# Revit family: CENTUM Gleitunterlage mit Abhebesicherung stehend_
name_source: partatom
category: HLS-Bauteile
revit_build: Autodesk Revit 2017 (Build: 20190508_0315(x64)
units: mm (PartAtom-declared; Revit-internal decimal feet)

## family parameters
Arbeitsebenenbasiert = Ja
Beim Laden mit Abzugskörper schneiden = Nein
Bemaßung runder Anschluss = Durchmesser verwenden
Gemeinsam genutzt = Ja
Immer vertikal = Nein
Raumberechnungspunkt = Nein
Teiletyp = Normal

## types (2) — shared parameters
Abhebesicherung = mit Abhebesicherung
Ausrichtung = stehend
Breite Gleitstreifen = 40 mm  [stored 0.131234 ft]
Breite Gleitunterlage = 115 mm  [stored 0.377297 ft]
C = 17 mm
Fabrikat = MEFA
Firma = MEFA Befestigungs- und Montagesysteme GmbH
Gleitreibungsfaktor = 0,15
Gleitstreifen = MEFA Gleitstreifen : Gleitstreifen  76x 40x 2
Haftreibungsfaktor = 0,2
Kurztext2 = stehend mit Abhebesicherung
Langloch = 14x40 mm
Länge Gleitstreifen = 76 mm  [stored 0.249344 ft]
Länge Gleitunterlage = 70 mm  [stored 0.229659 ft]
Mengeneinheit = SET
Sicherheitsfaktor = 1.54
Stärke = 16 mm  [stored 0.0524934 ft]
Vorgabe-Ansicht = 1219 mm
max. Stärke Gleitplatte = 16 mm  [stored 0.0524934 ft]
max. Temperaturbeständigkeit = 80 °C
max. zul. Last (Paar) = 40 kN
vpe = 1 SET

## per-type parameters (varying)
| type | Abhebesicherungslasche | Artikelnummer | EAN | Einfachanschluss | Gewicht | Gewicht pro Bauteil | Höhe | Höhe Gleitunterlage | Kurztext1 | Profiltyp |
| CENTUM Gleitunterlage mit Abhebesicherung XL100/XL200 stehend | Abhebesicherungslasche CENTUM : Abhebesicherungslasche XL100 (9000654) | 1651001020 | 4250928437228 | TL-XL Einfachanschluss stehend : Einfachanschluss XL100 stehend (9000594) | 2.13 kg | 2.13 kg | 110 mm | 74 mm | Gleitunterlage CENTUM XL 100 | XL 100, XL 200 |
| CENTUM Gleitunterlage mit Abhebesicherung XL120 stehend | Abhebesicherungslasche CENTUM : Abhebesicherungslasche XL120 (9000655) | 1651201050 | 4250928437259 | TL-XL Einfachanschluss stehend : Einfachanschluss XL120 stehend hoch (9000595) | 2.23 kg | 2.23 kg | 120 mm | 84 mm | Gleitunterlage CENTUM XL 120 | XL 120 |

note: [stored X ft] marks values corroborated as IEEE doubles in the binary element streams (Revit-internal decimal feet)

## geometry (parser evidence)
native form markers: Sweep x3
no freeform markers — native parametric forms only
